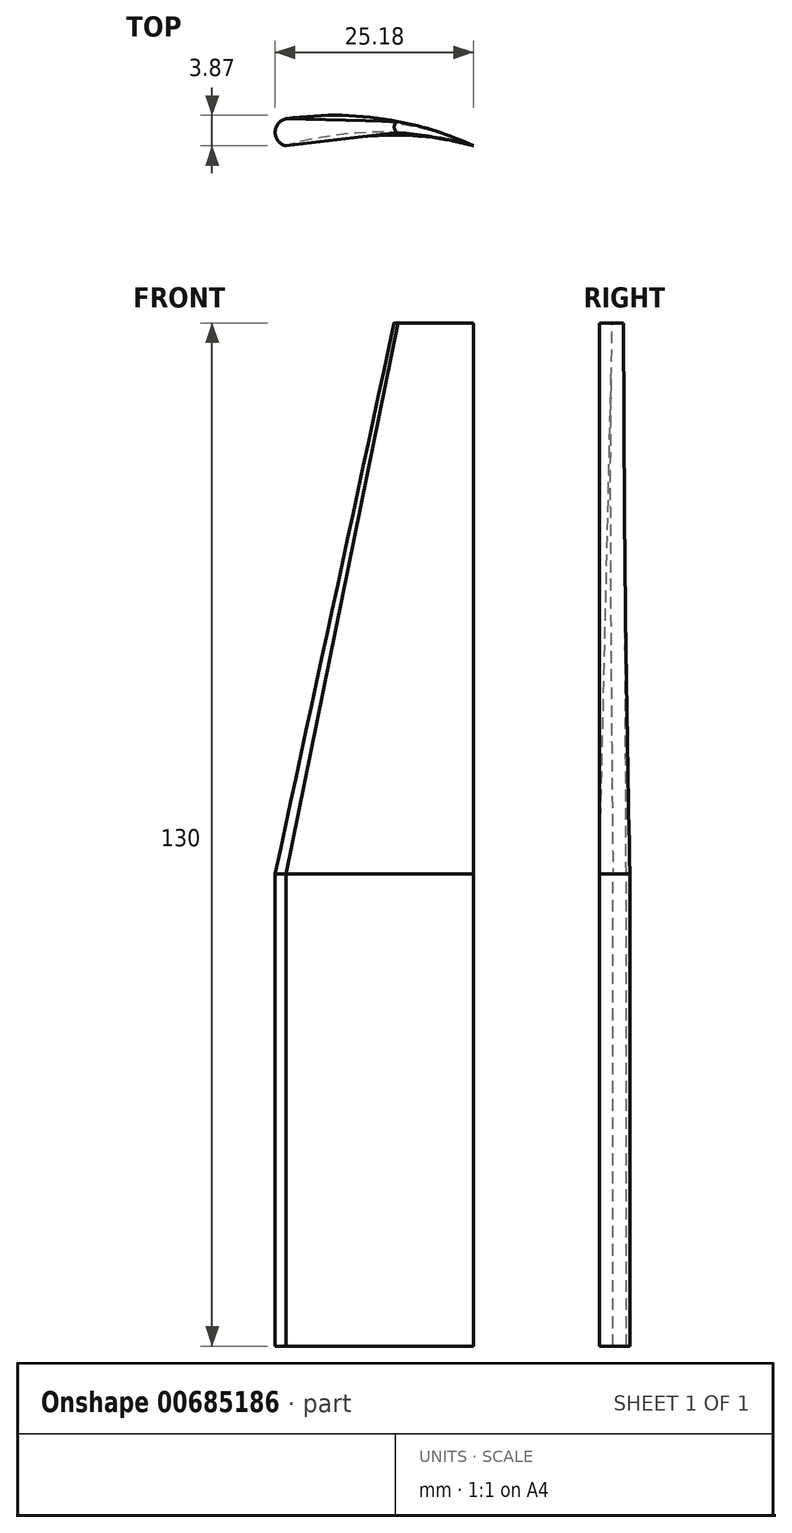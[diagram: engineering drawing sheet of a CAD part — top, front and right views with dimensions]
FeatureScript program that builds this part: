
annotation { "Feature Type Name" : "Feature", "Feature Type Description" : "" }
export const myFeature = defineFeature(function(context is Context, id is Id, definition is map)
    precondition{}
    {
        {
            var Q0;
            Q0=qCreatedBy(makeId("Top.planeOp"),FACE);
            var sketch = newSketch(context, id + "F0", { "sketchPlane" : qUnion([Q0])});
            skArc(sketch, "E0", {"start": v(23.81, -3.42) * mm, "mid": v(12.15, 0.02) * mm, "end": v(0, 0) * mm});
            skArc(sketch, "E1", {"start": v(23.81, -3.42) * mm, "mid": v(11.9, -1.7) * mm, "end": v(0, -3.42) * mm});
            skArc(sketch, "E2", {"start": v(0, 0) * mm, "mid": v(-1.37, -1.71) * mm, "end": v(0, -3.42) * mm});
            skSolve(sketch);
        }
        {
            var Q0;
            Q0=makeQuery(id+"F0.imprint","IMPRINT",FACE,{"disambiguationData":[TD([[makeQuery(id+"F0.imprint","IMPRINT",EDGE,{"derivedFrom":sQuery(id+"F0.wireOp",EDGE,"E0")}),1.0]])]});
            cPlane(context, id + "F1", {"entities" : qUnion([Q0]), "cplaneType" : CPlaneType.OFFSET, "offset" : 60 * mm, "width" : 150 * mm, "height" : 150 * mm});
        }
        {
            var Q0;
            Q0=qCreatedBy(id+"F1.planeOp",FACE);
            var sketch = newSketch(context, id + "F2", { "sketchPlane" : qUnion([Q0])});
            skArc(sketch, "E3.0", {"start": v(0, 0) * mm, "mid": v(-1.37, -1.71) * mm, "end": v(0, -3.42) * mm});
            skArc(sketch, "E3.1", {"start": v(23.81, -3.42) * mm, "mid": v(12.15, 0.02) * mm, "end": v(0, 0) * mm});
            skArc(sketch, "E3.2", {"start": v(23.81, -3.42) * mm, "mid": v(11.9, -1.7) * mm, "end": v(0, -3.42) * mm});
            skSolve(sketch);
        }
        {
            var Q0;
            Q0=qCreatedBy(id+"F1.planeOp",FACE);
            cPlane(context, id + "F3", {"entities" : qUnion([Q0]), "cplaneType" : CPlaneType.OFFSET, "offset" : 70 * mm, "width" : 150 * mm, "height" : 150 * mm});
        }
        {
            var Q0;
            Q0=qCreatedBy(id+"F3.planeOp",FACE);
            var sketch = newSketch(context, id + "F4", { "sketchPlane" : qUnion([Q0])});
            skArc(sketch, "E4.0", {"start": v(23.81, -3.42) * mm, "mid": v(12.15, 0.02) * mm, "end": v(0, 0) * mm, "construction": true});
            skArc(sketch, "E5.0", {"start": v(23.81, -3.42) * mm, "mid": v(11.9, -1.7) * mm, "end": v(0, -3.42) * mm, "construction": true});
            skArc(sketch, "E6", {"start": v(14.22, -0.33) * mm, "mid": v(13.75, -1.05) * mm, "end": v(14.22, -1.76) * mm});
            skArc(sketch, "E7", {"start": v(23.81, -3.42) * mm, "mid": v(19.05, -2.37) * mm, "end": v(14.22, -1.76) * mm});
            skArc(sketch, "E8", {"start": v(23.81, -3.42) * mm, "mid": v(19.1, -1.58) * mm, "end": v(14.22, -0.33) * mm});
            skSolve(sketch);
        }
        {
            var Q0;
            Q0=makeQuery(id+"F0.imprint","IMPRINT",FACE,{"disambiguationData":[TD([[makeQuery(id+"F0.imprint","IMPRINT",EDGE,{"derivedFrom":sQuery(id+"F0.wireOp",EDGE,"E0")}),1.0]])]});
            var Q1;
            Q1=makeQuery(id+"F2.imprint","IMPRINT",FACE,{"disambiguationData":[TD([[makeQuery(id+"F2.imprint","IMPRINT",EDGE,{"derivedFrom":sQuery(id+"F2.wireOp",EDGE,"E3.0")}),1.0]])]});
            loft(context, id + "F5", {"sheetProfilesArray" : [{ "sheetProfileEntities" : qUnion([Q0]) }, { "sheetProfileEntities" : qUnion([Q1]) }]});
        }
        {
            var Q0;
            Q0=makeQuery(id+"F5.opLoft","CAP_FACE",FACE,{"disambiguationData":[OSD([makeQuery(id+"F2.imprint","IMPRINT",FACE,{"disambiguationData":[TD([[makeQuery(id+"F2.imprint","IMPRINT",EDGE,{"derivedFrom":sQuery(id+"F2.wireOp",EDGE,"E3.0")}),1.0]])]})])],"isStart":true});
            var Q1;
            Q1=makeQuery(id+"F4.imprint","IMPRINT",FACE,{"disambiguationData":[TD([[makeQuery(id+"F4.imprint","IMPRINT",EDGE,{"derivedFrom":sQuery(id+"F4.wireOp",EDGE,"E6")}),1.0]])]});
            loft(context, id + "F6", {"sheetProfilesArray" : [{ "sheetProfileEntities" : qUnion([Q0]) }, { "sheetProfileEntities" : qUnion([Q1]) }]});
        }
    });
